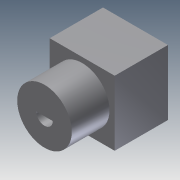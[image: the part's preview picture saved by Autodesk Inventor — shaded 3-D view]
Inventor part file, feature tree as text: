
AUTODESK INVENTOR PART (.ipt)
format: ipt  version: 2011 (Build 150239000, 239)  size: 118,784 bytes
history: native  units: in
note: dims shown in document units (in); Inventor stores cm internally (conversion verified against a paired STEP export)
features: extrude x8, sketch x8
ambient origin geometry x8: Origin, YZ Plane, XZ Plane, XY Plane, X Axis, Y Axis, Z Axis, Center Point
bodies: Solid1 (feature_tree)
feature tree (16):
  extrude  "Extrusion1"  Depth=1.9685in
  extrude  "Extrusion2"  Depth=1.6535in
  extrude  "Extrusion3"  Depth=0.5in
  extrude  "Extrusion4"  Depth=0.8268in TaperAngle=0.0deg
  extrude  "Extrusion5"  Depth=0.315in TaperAngle=0.0deg
  extrude  "Extrusion6"  Depth=0.1969in
  extrude  "Extrusion7"  Depth=0.1969in
  extrude  "Extrusion8"  Depth=0.0394in
  sketch  "Sketch1"  dims[d0=1.9685in d1=1.9685in]
  sketch  "Sketch2"  dims[d2=1.6142in d3=0.0in d4=1.6535in]
  sketch  "Sketch3"  dims[d5=1.1417in d6=0.0in d7=0.5in]
  sketch  "Sketch4"  dims[d8=1.1417in d9=0.0in d10=0.8268in d11=0.0in]
  sketch  "Sketch5"  dims[d12=0.0394in d13=0.0in d14=0.315in d15=0.0in]
  sketch  "Sketch6"  dims[d16=0.0394in d17=0.0in d18=0.1969in]
  sketch  "Sketch7"  dims[d19=0.1969in d20=0.1969in]
  sketch  "Sketch8"  dims[d21=0.1969in d22=0.0394in d23=0.0394in d24=0.2362in d25=0.0in]
